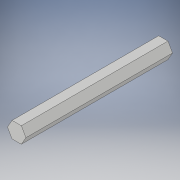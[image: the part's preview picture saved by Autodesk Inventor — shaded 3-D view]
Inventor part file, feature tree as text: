
AUTODESK INVENTOR PART (.ipt)
format: ipt  version: 2018 (Build 220112000, 112)  size: 94,208 bytes
history: native  units: in
note: dims shown in document units (in); Inventor stores cm internally (conversion verified against a paired STEP export)
features: extrude x1, sketch x1
ambient origin geometry x8: Origin, YZ Plane, XZ Plane, XY Plane, X Axis, Y Axis, Z Axis, Center Point
bodies: Solid1 (feature_tree)
feature tree (2):
  extrude  "Extrusion1"  Depth=4.572in TaperAngle=0.0deg
  sketch  "Sketch1"  dims[d0=0.5in d1=4.572in d2=0.0in]
